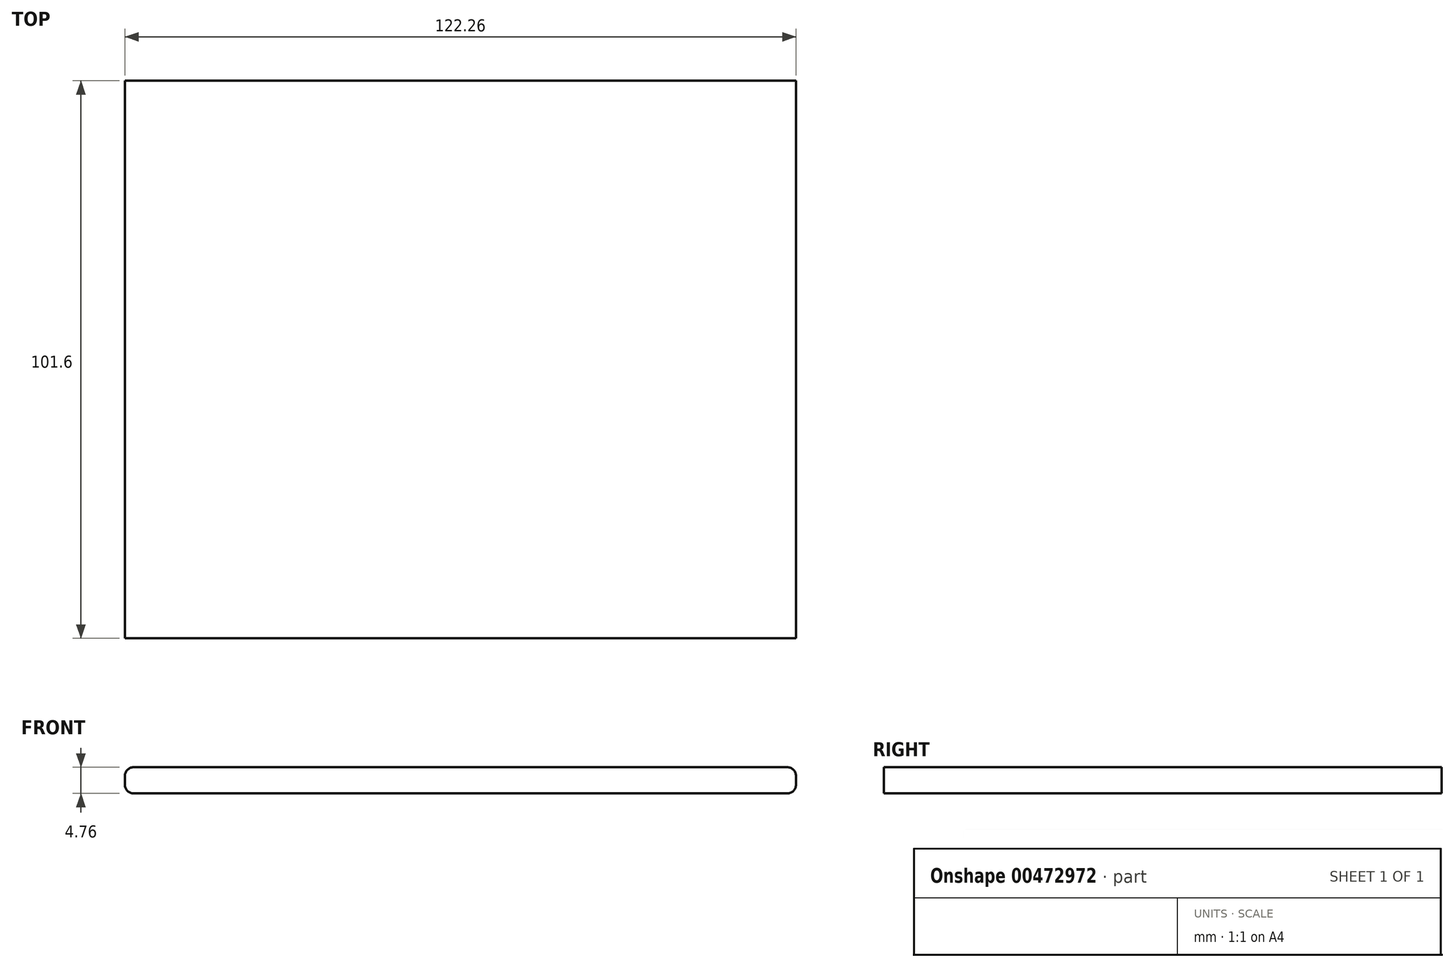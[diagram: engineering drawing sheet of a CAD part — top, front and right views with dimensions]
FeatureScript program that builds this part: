
annotation { "Feature Type Name" : "Feature", "Feature Type Description" : "" }
export const myFeature = defineFeature(function(context is Context, id is Id, definition is map)
    precondition{}
    {
        {
            var Q0;
            Q0=qCreatedBy(makeId("Top.planeOp"),FACE);
            var sketch = newSketch(context, id + "F0", { "sketchPlane" : qUnion([Q0])});
            skLineSegment(sketch, "E0.bottom", {"start": v(61.13, -50.8) * mm, "end": v(-61.13, -50.8) * mm});
            skLineSegment(sketch, "E0.top", {"start": v(61.13, 50.8) * mm, "end": v(-61.13, 50.8) * mm});
            skLineSegment(sketch, "E0.left", {"start": v(61.13, -50.8) * mm, "end": v(61.13, 50.8) * mm});
            skLineSegment(sketch, "E0.right", {"start": v(-61.13, -50.8) * mm, "end": v(-61.13, 50.8) * mm});
            skPoint(sketch, "E0.middle", {"position": v(0, 0) * mm});
            skSolve(sketch);
        }
        {
            var Q0;
            Q0 = qSketchRegion(id + "F0", true);
            extrude(context, id + "F1", {"entities" : qUnion([Q0]), "depth" : 4.76 * mm});
        }
        {
            var Q0;
            Q0=makeQuery(id+"F1.opExtrude","CAP_EDGE",EDGE,{"disambiguationData":[OSD([sQuery(id+"F0.wireOp",EDGE,"E0.right")])],"isStart":true});
            var Q1;
            Q1=makeQuery(id+"F1.opExtrude","CAP_EDGE",EDGE,{"disambiguationData":[OSD([sQuery(id+"F0.wireOp",EDGE,"E0.right")])],"isStart":false});
            var Q2;
            Q2=makeQuery(id+"F1.opExtrude","CAP_EDGE",EDGE,{"disambiguationData":[OSD([sQuery(id+"F0.wireOp",EDGE,"E0.left")])],"isStart":false});
            var Q3;
            Q3=makeQuery(id+"F1.opExtrude","CAP_EDGE",EDGE,{"disambiguationData":[OSD([sQuery(id+"F0.wireOp",EDGE,"E0.left")])],"isStart":true});
            fillet(context, id + "F2", {"entities" : qUnion([Q0, Q1, Q2, Q3]), "radius" : 1.59 * mm, "tangentPropagation" : true, "allowEdgeOverflow" : false});
        }
    });
